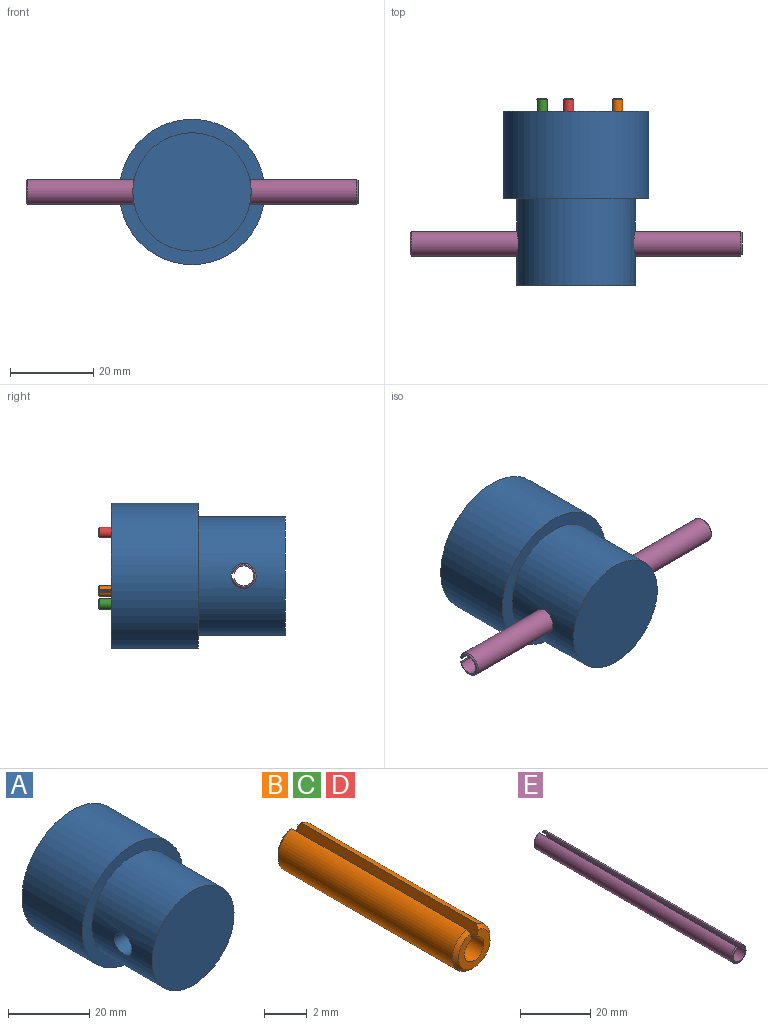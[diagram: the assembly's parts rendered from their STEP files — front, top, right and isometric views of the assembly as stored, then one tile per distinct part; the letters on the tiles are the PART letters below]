
ASSEMBLY  parts=5 mates=4
PART A: 12 faces, bbox 35x42x35 mm
  f0: cylinder r=14.25mm len=28.5mm, axis (0,1,0), area 1823.3mm2, adj f2,f4,f5
  f1: cylinder r=17.5mm len=35mm, axis (0,1,0), area 2309.1mm2, adj f2,f3
  f2: plane 35x35mm, normal (0,-1,0), area 324.2mm2, adj f0,f1
  f3: plane 35x35mm, normal (0,1,0), area 947.4mm2, adj f1,f6,f8,f10
  f4: plane 28.5x28.5mm, normal (0,-1,0), area 637.9mm2, adj f0
  f5: cylinder r=3mm len=28.5mm, axis (-1,0,0), area 531.2mm2, adj f0
  f6: cylinder r=1.25mm len=8.75mm, axis (0,1,0), area 68.7mm2, adj f3,f7
  f7: plane 2.5x2.5mm, normal (0,1,0), area 4.9mm2, adj f6
  f8: cylinder r=1.25mm len=8.75mm, axis (0,1,0), area 68.7mm2, adj f3,f9
  f9: plane 2.5x2.5mm, normal (0,1,0), area 4.9mm2, adj f8
  f10: cylinder r=1.25mm len=8.75mm, axis (0,1,0), area 68.7mm2, adj f3,f11
  f11: plane 2.5x2.5mm, normal (0,1,0), area 4.9mm2, adj f10
PART B: 8 faces, bbox 2.5x12x2.5 mm
  f0: cylinder r=1.25mm len=11.6mm, axis (0,1,0), area 83.5mm2, adj f4,f5,f6,f7
  f1: plane 2.1x2.06mm, normal (0,-1,0), area 2mm2, adj f3,f4,f6,f7
  f2: plane 2.1x2.06mm, normal (0,1,0), area 2mm2, adj f3,f5,f6,f7
  f3: cylinder r=0.65mm len=12mm, axis (0,1,0), area 44.9mm2, adj f1,f2,f6,f7
  f4: cone r=1.05mm half-angle=45deg, axis (0,1,0), area 1.9mm2, adj f0,f1,f6,f7
  f5: cone r=1.25mm half-angle=45deg, axis (0,-1,0), area 1.9mm2, adj f0,f2,f6,f7
  f6: plane 12x0.58mm, normal (-0.97,0,0.26), area 7.2mm2, adj f0,f1,f2,f3,f4,f5
  f7: plane 12x0.58mm, normal (0.97,0,0.26), area 7.2mm2, adj f0,f1,f2,f3,f4,f5
PART C: same geometry as B
PART D: same geometry as B
PART E: 8 faces, bbox 6x80x5.9 mm
  f0: cylinder r=3mm len=79.4mm, axis (0,1,0), area 1371.9mm2, adj f4,f5,f6,f7
  f1: plane 5.4x5.31mm, normal (0,-1,0), area 4.4mm2, adj f3,f4,f6,f7
  f2: plane 5.4x5.31mm, normal (0,1,0), area 4.4mm2, adj f3,f5,f6,f7
  f3: cylinder r=2.4mm len=80mm, axis (0,1,0), area 1105.8mm2, adj f1,f2,f6,f7
  f4: cone r=2.7mm half-angle=45deg, axis (0,1,0), area 7mm2, adj f0,f1,f6,f7
  f5: cone r=3mm half-angle=45deg, axis (0,-1,0), area 7mm2, adj f0,f2,f6,f7
  f6: plane 80x0.58mm, normal (-0.97,0,0.26), area 47.9mm2, adj f0,f1,f2,f3,f4,f5
  f7: plane 80x0.58mm, normal (0.97,0,0.26), area 47.9mm2, adj f0,f1,f2,f3,f4,f5
PLACE A t=(-14.48,6.27,-9.56)mm
PLACE B rot(axis=(0,-1,0),90deg) t=(-4.51,9.32,-13.24)mm
PLACE C rot(axis=(0,1,0),90deg) t=(-22.64,9.32,-16.36)mm
PLACE D rot(axis=(0,1,0),180deg) t=(-16.28,9.32,0.9)mm
PLACE E rot(axis=(-0.58,0.58,0.58),120deg) t=(-54.48,-25.67,-9.56)mm
MATE fastened B.f0 <-> A.f8  axis (0,1,0) through (-4.51,-2.48,-13.24)mm
MATE fastened D.f0 <-> A.f10  axis (0,-1,0) through (-16.28,-2.48,0.9)mm
MATE fastened C.f0 <-> A.f6  axis (0,1,0) through (-22.64,-2.48,-16.36)mm
MATE fastened E.f0 <-> A.f5  axis (-1,0,0) through (-14.48,-25.67,-9.56)mm
